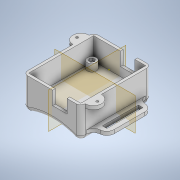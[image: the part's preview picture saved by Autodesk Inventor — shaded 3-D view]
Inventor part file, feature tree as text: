
AUTODESK INVENTOR PART (.ipt)
format: ipt  version: 2021 (Build 250183000, 183)  size: 416,256 bytes
history: native  units: mm
features: extrude x19, sketch x17, fillet x7, mirror x5, plane x2, pattern_linear x1, projected_geometry x1
ambient origin geometry x8: Origin, YZ Plane, XZ Plane, XY Plane, X Axis, Y Axis, Z Axis, Center Point
bodies: Solid1 (feature_tree)
feature tree (52):
  sketch  "Sketch1"  dims[d0=76.0mm d1=90.0mm]
  extrude  "Extrusion2"  Depth=90.0mm
  extrude  "Extrusion3"  Depth=3.0mm TaperAngle=0.0deg
  extrude  "Extrusion4"  Depth=10.0mm
  extrude  "Extrusion5"  Depth=8.0mm TaperAngle=0.0deg
  pattern_linear  "Rectangular Pattern1"  Count1=2 Spacing1=56.07mm
  sketch  "Sketch5"  dims[d12=6.0mm]
  extrude  "Extrusion6"  Depth=9.0mm TaperAngle=0.0deg
  extrude  "Extrusion7"  Depth=24.5mm TaperAngle=0.0deg
  sketch  "Sketch6"  dims[d13=2.7mm d14=0.0mm]
  extrude  "Extrusion8"  Depth=3.0mm TaperAngle=0.0deg
  extrude  "Extrusion9"  Depth=3.0mm TaperAngle=0.0deg
  plane  "Work Plane1"
  mirror  "Mirror1"
  sketch  "Sketch14"  dims[d15=3.3mm]
  extrude  "Extrusion15"  Depth=18.0mm
  extrude  "Extrusion17"  Depth=10.0mm TaperAngle=0.0deg
  extrude  "Extrusion18"  Depth=4.0mm TaperAngle=0.0deg
  mirror  "Mirror5"
  plane  "Work Plane3"
  mirror  "Mirror6"
  extrude  "Extrusion22"  Depth=4.0mm
  fillet  "Fillet9"  Radius=4.0mm
  extrude  "Extrusion23"  Depth=3.0mm
  extrude  "Extrusion24"  Depth=15.0mm
  fillet  "Fillet10"  Radius=15.0mm
  mirror  "Mirror8"
  fillet  "Fillet11"  Radius=40.0mm
  extrude  "Extrusion25"  Depth=5.0mm
  extrude  "Extrusion19"  Depth=5.0mm
  extrude  "Extrusion20"  Depth=15.0mm TaperAngle=0.0deg
  extrude  "Extrusion21"  Depth=3.0mm
  fillet  "Fillet5"  Radius=3.0mm
  fillet  "Fillet6"  Radius=3.0mm
  mirror  "Mirror7"
  fillet  "Fillet7"  Radius=3.0mm
  fillet  "Fillet8"  Radius=70.0mm
  extrude  "Extrusion1"  Depth=10.0mm TaperAngle=0.0deg
  sketch  "Sketch2"  dims[d2=3.0mm d3=30.0mm d4=0.0mm]
  sketch  "Sketch3"  dims[d5=3.0mm d6=0.0mm d7=10.0mm]
  sketch  "Sketch4"  dims[d8=3.0mm d10=8.0mm d11=0.0mm]
  sketch  "Sketch15"  dims[d16=9.0mm d17=0.0mm d18=20.0mm d20=56.07mm d21=20.0mm d23=45.71mm]
  projected_geometry  "Projected Loop3"
  sketch  "Sketch19"  dims[d24=5.0mm d25=9.0mm d26=0.0mm]
  sketch  "Sketch20"  dims[d27=3.0mm d28=24.5mm d29=0.0mm]
  sketch  "Sketch21"  dims[d30=16.0mm d31=3.0mm d32=0.0mm]
  sketch  "Sketch22"  dims[d36=16.0mm d37=3.0mm d38=0.0mm]
  sketch  "Sketch23"  dims[d39=18.0mm d62=6.68mm]
  sketch  "Sketch24"  dims[d63=1.7mm d64=10.0mm d65=0.0mm]
  sketch  "Sketch25"  dims[d71=9.0mm d72=4.0mm d73=0.0mm]
  sketch  "Sketch26"  dims[d74=2.5mm d75=4.5mm d76=4.0mm d77=0.0mm]
  sketch  "Sketch27"  dims[d78=4.0mm d79=0.0mm d80=3.0mm d81=50.0mm d82=15.0mm d83=0.0mm d84=40.0mm d85=5.0mm d86=5.0mm d87=20.0mm d88=0.0mm d89=3.0mm d90=3.0mm d91=3.0mm d92=3.0mm d93=70.0mm d94=10.0mm d95=0.0mm d96=5.0mm d97=50.0mm d98=4.0mm d99=15.0mm d100=0.0mm d101=40.0mm d102=5.0mm d103=5.0mm d104=15.0mm d105=0.0mm d106=8.0mm d107=8.0mm d108=15.0mm d109=0.0mm]
